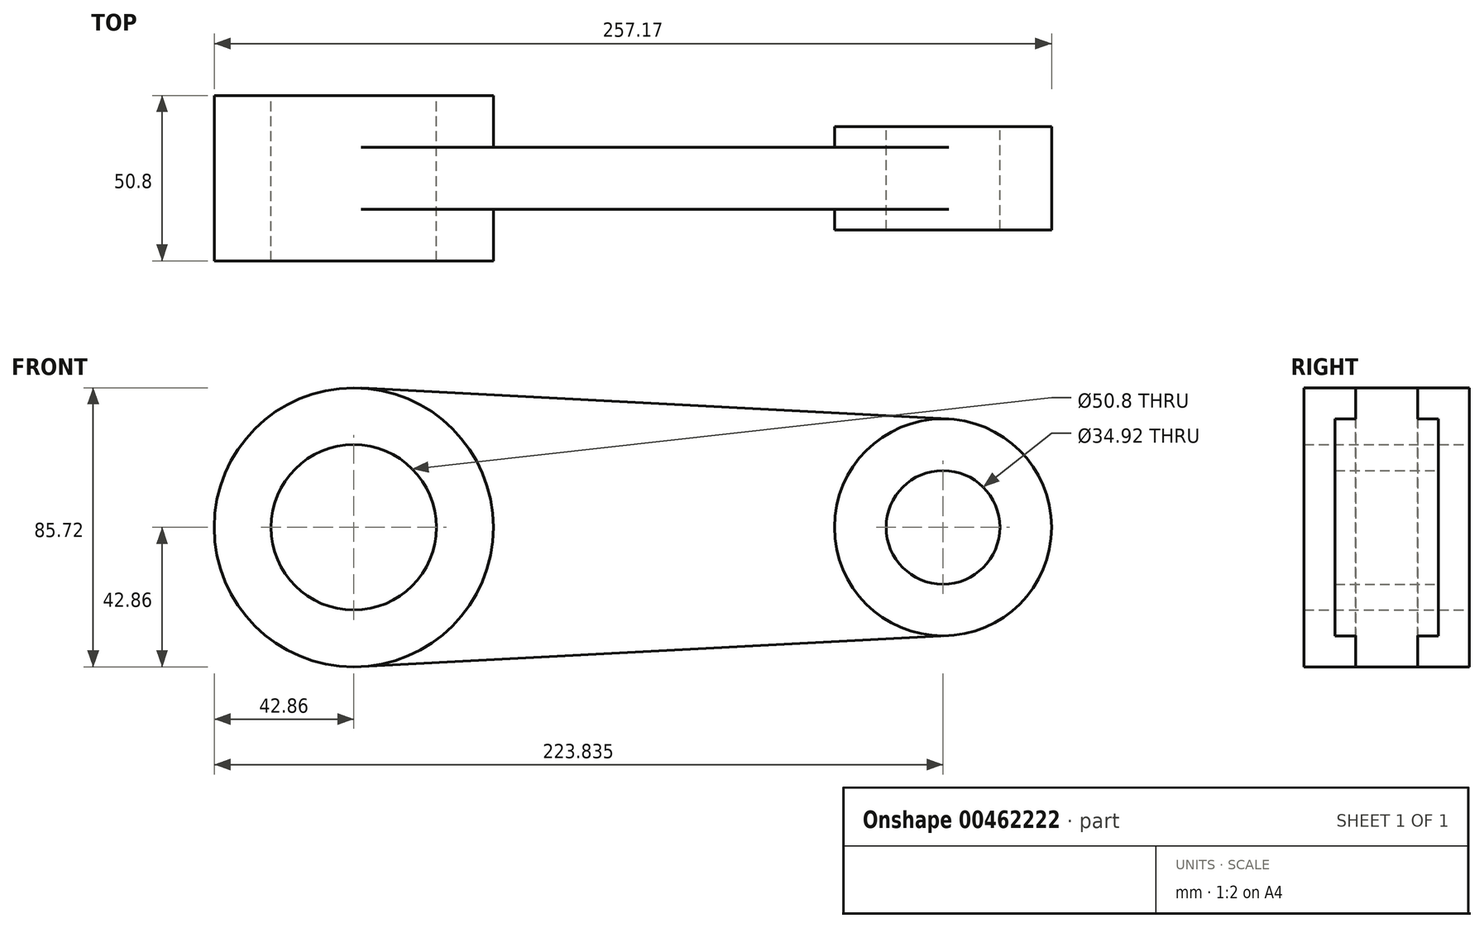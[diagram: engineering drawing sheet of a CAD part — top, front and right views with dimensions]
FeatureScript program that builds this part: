
annotation { "Feature Type Name" : "Feature", "Feature Type Description" : "" }
export const myFeature = defineFeature(function(context is Context, id is Id, definition is map)
    precondition{}
    {
        {
            var Q0;
            Q0=qCreatedBy(makeId("Front.planeOp"),FACE);
            var sketch = newSketch(context, id + "F0", { "sketchPlane" : qUnion([Q0])});
            skCircle(sketch, "E0", {"center": v(0, 0) * mm, "radius": 25.4 * mm});
            skCircle(sketch, "E1", {"center": v(0, 0) * mm, "radius": 42.86 * mm});
            skCircle(sketch, "E2", {"center": v(180.98, 0) * mm, "radius": 17.46 * mm});
            skCircle(sketch, "E3", {"center": v(180.98, 0) * mm, "radius": 33.34 * mm});
            skLineSegment(sketch, "E4", {"start": v(2.26, 42.8) * mm, "end": v(182.73, 33.3) * mm});
            skLineSegment(sketch, "E5.MirrorCS", {"start": v(2.26, -42.8) * mm, "end": v(182.73, -33.3) * mm});
            skSolve(sketch);
        }
        {
            var Q0;
            Q0=makeQuery(id+"F0.imprint","IMPRINT",FACE,{"disambiguationData":[TD([[makeQuery(id+"F0.imprint","IMPRINT",EDGE,{"derivedFrom":sQuery(id+"F0.wireOp",EDGE,"E0")}),-1.0]])]});
            extrude(context, id + "F1", {"entities" : qUnion([Q0]), "depth" : 50.8 * mm, "symmetric" : true});
        }
        {
            var Q0;
            {var subQ0=sQuery(id+"F0.wireOp",EDGE,"E4");Q0=makeQuery(id+"F0.imprint","IMPRINT",FACE,{"disambiguationData":[TD([[makeQuery(id+"F0.imprint","IMPRINT",EDGE,{"derivedFrom":subQ0}),-1.0]])]});}
            extrude(context, id + "F2", {"entities" : qUnion([Q0]), "operationType" : NewBodyOperationType.ADD, "depth" : 19.05 * mm, "symmetric" : true});
        }
        {
            var Q0;
            Q0=makeQuery(id+"F0.imprint","IMPRINT",FACE,{"disambiguationData":[TD([[makeQuery(id+"F0.imprint","IMPRINT",EDGE,{"derivedFrom":sQuery(id+"F0.wireOp",EDGE,"E2")}),-1.0]])]});
            extrude(context, id + "F3", {"entities" : qUnion([Q0]), "operationType" : NewBodyOperationType.ADD, "depth" : 31.75 * mm, "symmetric" : true});
        }
    });
